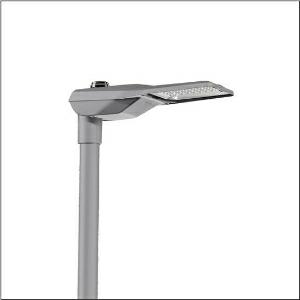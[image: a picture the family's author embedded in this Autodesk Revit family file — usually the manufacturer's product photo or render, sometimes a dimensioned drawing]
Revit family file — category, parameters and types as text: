
# Revit family: streetlight_sl_21_mini___st1_0a_5xe6d37n08jb_4401
name_source: partatom
category: Lighting Fixtures
units: mm (PartAtom-declared; Revit-internal decimal feet)

## family parameters
Cut with Voids When Loaded = No
Host = Face
Light Source = No
Part Type = Normal
Room Calculation Point = No
Round Connector Dimension = Use Diameter
Shared = No

## types (1)
- --- (1 x LED, 12830 lm, 87.3 W, 3000K)
    Apparent Load = 87 VA
    CIE Flux Codes = 40 73 97 100 100
    Color Rendering = 70
    Color Temperature = 3000K
    Default Elevation = 1800 mm
    Description = Streetlight SL 21 mini, mast luminaire, primary light control with lens, of PMMA, primary optical cover: cover, of toughened safety glass, transparent, light distribution: ST1.0a, light emission: direct distribution, primary light characteristic: asymmetric, installation type: side-entry, LED, 3G 2.5mm², High Power LED, rated luminous flux: 12.830lm, luminous efficacy: 147lm/W, light colour: 730, colour temperature: 3000K, control gear: NEMA (7pin), control: overheat protection, pre-setting: linear dimming characteristic, constant luminous flux control, time-dependent luminous flux control, flexible luminous flux parameterisation, mains connection: 230..240V, AC, 50/60Hz, connection cable pre-assembled, cable length: 10,5m, wiring characteristics: H05VV-F, start of lifetime: 87W, end of service life: 90W, reduction: 40W, luminaire housing, of diecast aluminium (EN AC-44300), powder-coated, Siteco® metallic grey (DB 702S), corrosivity category C5 mid according to DIN EN ISO 12944, multi-level sealing system, sealing non-destructively replaceable, inclination adjustable: 0°, 5°, 10°, 15°, length: 628mm, width: 235mm, height: 110mm, spigot size: 42mm (side-entry), mounting height: 4..8m, protection rating (complete): IP66, insulation class (complete): insulation class I (protective earthing), certification: CE, ENEC, ENEC+, VDE, impact resistance: IK10, permissible operating ambient temperature for outdoor applications: -40..+50°C, standard-compliant lighting for roads and squares, packaging unit: 1 piece

Light Distribution: ST1.0a
    Height = 110 mm
    Lamp = 1 x LED
    Lamp Light Flux = 12830 lm
    Lamp Power = 87.3 W
    Lamp count = 1
    Length = 625 mm
    Luminous efficacy = 147 lm/W
    Manufacturer = Siteco
    ModVariant = No
    Model = 5XE6D37N08JB
    Number of Poles = 1
    OnlyDefault = Yes
    Power Factor = 1
    Product Name = Streetlight SL 21 mini | ST1.0a
    Product group = mast luminaire | pylon top
    ProductGroupID = 6100
    Protection Class = Protection class I
    Protection Degree = IP 66
    RLX_Detail_Level = 1
    RLX_Emergency_Light_Flux = 0 lm
    RLX_Emergency_Type = 0
    RLX_Emergency_Type_DB = No
    RlxData = <blob elided: 26113 chars, md5=d5e7de67>
    Socket = socket
    Standby Power = 0 W
    System Light Flux = 12830 lm
    System Power = 87 W
    Type Comments = factory setting: luminous flux: 100 % | dim-lin: 254 | 915 mA
    Type Image = l_1294379.jpg
    URL = http://relux.com
    VarID = @adj_156841
    Voltage = 0 V
    Weight = 0.00 kg
    Width = 234 mm

## geometry (parser evidence)
native form markers: Blend x4, Sweep x9
no freeform markers — native parametric forms only
